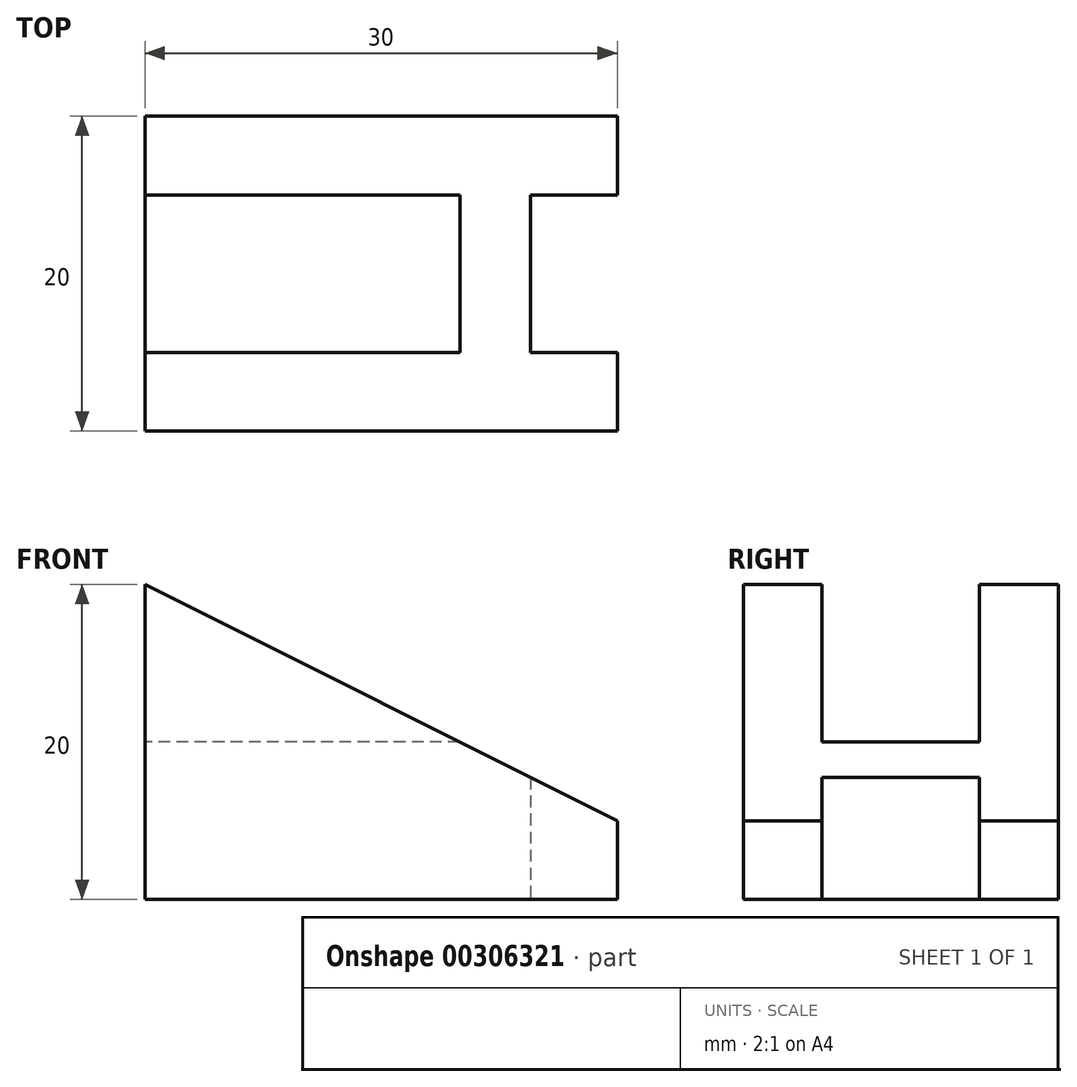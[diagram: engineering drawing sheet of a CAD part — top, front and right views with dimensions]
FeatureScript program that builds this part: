
annotation { "Feature Type Name" : "Feature", "Feature Type Description" : "" }
export const myFeature = defineFeature(function(context is Context, id is Id, definition is map)
    precondition{}
    {
        {
            var Q0;
            Q0=qCreatedBy(makeId("Front.planeOp"),FACE);
            var sketch = newSketch(context, id + "F0", { "sketchPlane" : qUnion([Q0])});
            skLineSegment(sketch, "E0", {"start": v(0, 0) * mm, "end": v(0, 20) * mm});
            skLineSegment(sketch, "E1", {"start": v(0, 0) * mm, "end": v(30, 0) * mm});
            skLineSegment(sketch, "E2", {"start": v(30, 0) * mm, "end": v(30, 5) * mm});
            skLineSegment(sketch, "E3", {"start": v(30, 5) * mm, "end": v(0, 20) * mm});
            skSolve(sketch);
        }
        {
            var Q0;
            Q0 = qSketchRegion(id + "F0", true);
            extrude(context, id + "F1", {"entities" : qUnion([Q0]), "depth" : 20 * mm});
        }
        {
            var Q0;
            Q0=makeQuery(id+"F1.opExtrude","SWEPT_FACE",FACE,{"disambiguationData":[OSD([sQuery(id+"F0.wireOp",EDGE,"E2")])]});
            var sketch = newSketch(context, id + "F2", { "sketchPlane" : qUnion([Q0])});
            skLineSegment(sketch, "E4", {"start": v(-15, 5) * mm, "end": v(-15, 0) * mm});
            skLineSegment(sketch, "E5", {"start": v(-15, 5) * mm, "end": v(-5, 5) * mm});
            skLineSegment(sketch, "E6", {"start": v(-15, 0) * mm, "end": v(-5, 0) * mm});
            skLineSegment(sketch, "E7", {"start": v(-5, 0) * mm, "end": v(-5, 5) * mm});
            skSolve(sketch);
        }
        {
            var Q0;
            Q0 = qSketchRegion(id + "F2", true);
            extrude(context, id + "F3", {"entities" : qUnion([Q0]), "operationType" : NewBodyOperationType.REMOVE, "oppositeDirection" : true, "depth" : 5.5 * mm});
        }
        {
            var Q0;
            Q0=makeQuery(id+"F1.opExtrude","SWEPT_FACE",FACE,{"disambiguationData":[OSD([sQuery(id+"F0.wireOp",EDGE,"E0")])]});
            var sketch = newSketch(context, id + "F4", { "sketchPlane" : qUnion([Q0])});
            skLineSegment(sketch, "E8", {"start": v(5, 20) * mm, "end": v(5, 10) * mm});
            skLineSegment(sketch, "E9", {"start": v(5, 10) * mm, "end": v(15, 10) * mm});
            skLineSegment(sketch, "E10", {"start": v(15, 10) * mm, "end": v(15, 20) * mm});
            skLineSegment(sketch, "E11", {"start": v(5, 20) * mm, "end": v(15, 20) * mm});
            skSolve(sketch);
        }
        {
            var Q0;
            Q0 = qSketchRegion(id + "F4", true);
            extrude(context, id + "F5", {"entities" : qUnion([Q0]), "operationType" : NewBodyOperationType.REMOVE, "endBound" : BoundingType.THROUGH_ALL, "oppositeDirection" : true, "depth" : 25 * mm});
        }
        {
            var Q0;
            Q0=makeQuery(id+"F3.boolean.opBoolean","COPY",FACE,{"derivedFrom":makeQuery(id+"F3.opExtrude","SWEPT_FACE",FACE,{"disambiguationData":[OSD([sQuery(id+"F2.wireOp",EDGE,"E5")])]})});
            var sketch = newSketch(context, id + "F6", { "sketchPlane" : qUnion([Q0])});
            skLineSegment(sketch, "E12", {"start": v(30, 15) * mm, "end": v(24.5, 15) * mm});
            skLineSegment(sketch, "E13", {"start": v(24.5, 15) * mm, "end": v(24.5, 5) * mm});
            skLineSegment(sketch, "E14", {"start": v(24.5, 5) * mm, "end": v(30, 5) * mm});
            skLineSegment(sketch, "E15", {"start": v(30, 5) * mm, "end": v(30, 15) * mm});
            skSolve(sketch);
        }
        {
            var Q0;
            Q0 = qSketchRegion(id + "F6", true);
            extrude(context, id + "F7", {"entities" : qUnion([Q0]), "operationType" : NewBodyOperationType.REMOVE, "endBound" : BoundingType.THROUGH_ALL, "oppositeDirection" : true, "depth" : 25 * mm});
        }
    });
